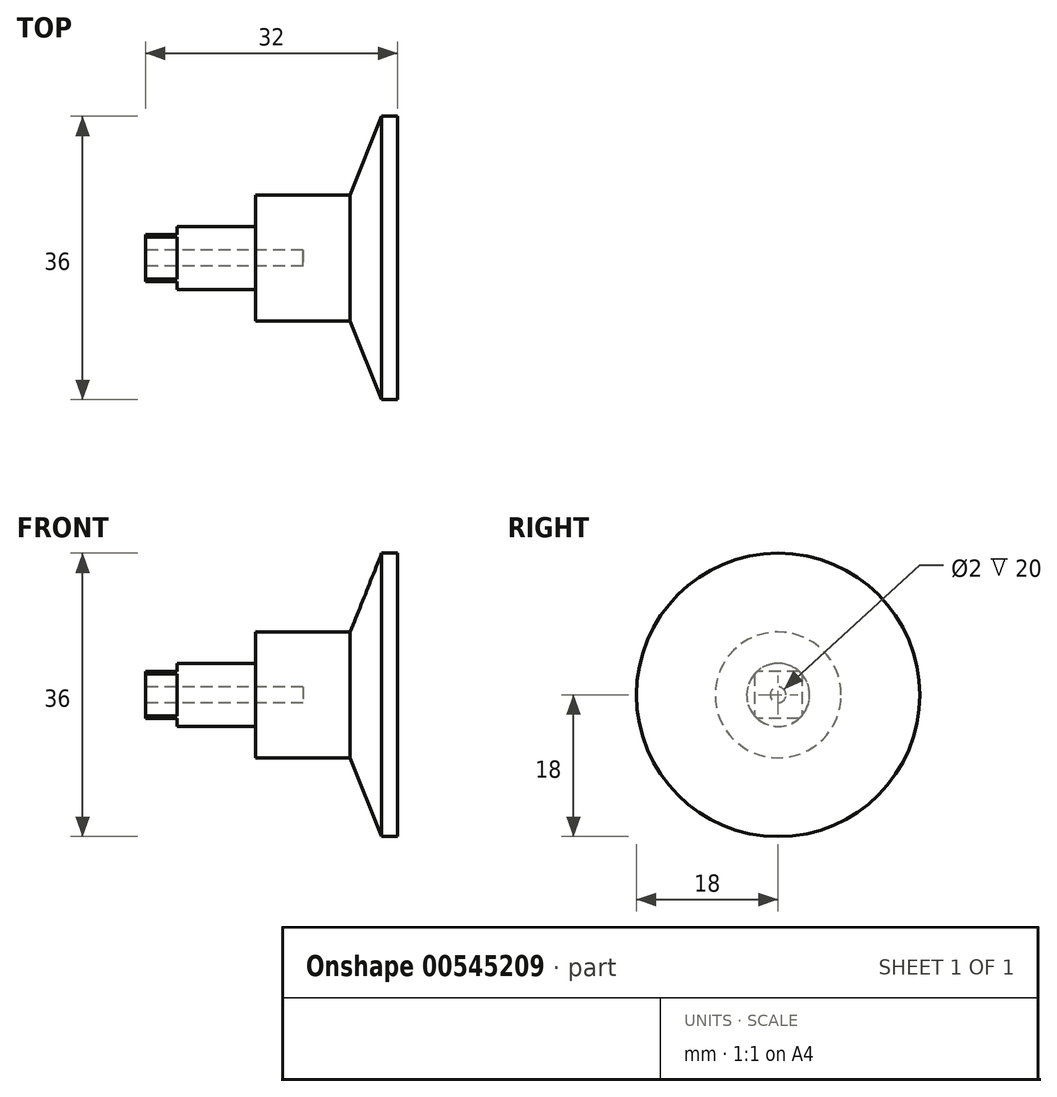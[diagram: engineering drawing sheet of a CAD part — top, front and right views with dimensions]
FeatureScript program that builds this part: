
annotation { "Feature Type Name" : "Feature", "Feature Type Description" : "" }
export const myFeature = defineFeature(function(context is Context, id is Id, definition is map)
    precondition{}
    {
        {
            var Q0;
            Q0=qCreatedBy(makeId("Front.planeOp"),FACE);
            var sketch = newSketch(context, id + "F0", { "sketchPlane" : qUnion([Q0])});
            skLineSegment(sketch, "E0", {"start": v(-44.44, 0) * mm, "end": v(44.44, 0) * mm, "construction": true});
            skLineSegment(sketch, "E1", {"start": v(-18, 8) * mm, "end": v(-6, 8) * mm});
            skLineSegment(sketch, "E2", {"start": v(-6, 8) * mm, "end": v(-2, 18) * mm});
            skLineSegment(sketch, "E3", {"start": v(-2, 18) * mm, "end": v(0, 18) * mm});
            skLineSegment(sketch, "E4", {"start": v(0, 18) * mm, "end": v(0, 0) * mm});
            skLineSegment(sketch, "E5", {"start": v(0, 0) * mm, "end": v(-12, 0) * mm});
            skLineSegment(sketch, "E6", {"start": v(-12, 0) * mm, "end": v(-12, 1) * mm});
            skLineSegment(sketch, "E7", {"start": v(-12, 1) * mm, "end": v(-32, 1) * mm});
            skLineSegment(sketch, "E8", {"start": v(-32, 1) * mm, "end": v(-32, 4) * mm});
            skLineSegment(sketch, "E9", {"start": v(-32, 4) * mm, "end": v(-18, 4) * mm});
            skLineSegment(sketch, "E10", {"start": v(-18, 4) * mm, "end": v(-18, 8) * mm});
            skSolve(sketch);
        }
        {
            var Q0;
            Q0 = qSketchRegion(id + "F0", true);
            var Q1;
            Q1=sQuery(id+"F0.wireOp",EDGE,"E0");
            revolve(context, id + "F1", {"entities" : qUnion([Q0]), "axis" : qUnion([Q1]), "revolveType" : RevolveType.FULL});
        }
        {
            var Q0;
            Q0=makeQuery(id+"F1.opRevolve","SWEPT_FACE",FACE,{"disambiguationData":[OSD([sQuery(id+"F0.wireOp",EDGE,"E8")])]});
            var sketch = newSketch(context, id + "F2", { "sketchPlane" : qUnion([Q0])});
            skLineSegment(sketch, "E11.bottom", {"start": v(-3, 3) * mm, "end": v(3, 3) * mm});
            skLineSegment(sketch, "E11.top", {"start": v(-3, -3) * mm, "end": v(3, -3) * mm});
            skLineSegment(sketch, "E11.left", {"start": v(-3, 3) * mm, "end": v(-3, -3) * mm});
            skLineSegment(sketch, "E11.right", {"start": v(3, 3) * mm, "end": v(3, -3) * mm});
            skCircle(sketch, "E12.0", {"center": v(0, 0) * mm, "radius": 4 * mm});
            skLineSegment(sketch, "E13", {"start": v(-3, -3) * mm, "end": v(3, 3) * mm, "construction": true});
            skSolve(sketch);
        }
        {
            var Q0;
            Q0=makeQuery(id+"F2.imprint","IMPRINT",FACE,{"disambiguationData":[TD([[makeQuery(id+"F2.imprint","IMPRINT",EDGE,{"derivedFrom":makeQuery(id+"F1.opRevolve","SWEPT_EDGE",EDGE,{"disambiguationData":[OSD([sQuery(id+"F0.wireOp",EDGE,"E7"),sQuery(id+"F0.wireOp",EDGE,"E8")])]})}),1.0]])]});
            var Q1;
            Q1=makeQuery(id+"F2.imprint","IMPRINT",FACE,{"disambiguationData":[TD([[makeQuery(id+"F2.imprint","IMPRINT",EDGE,{"derivedFrom":sQuery(id+"F2.wireOp",EDGE,"E11.bottom")}),1.0]])]});
            var Q2;
            {var subQ0=sQuery(id+"F2.wireOp",EDGE,"E12.0");var subQ1=sQuery(id+"F2.wireOp",EDGE,"E11.right");var subQ2=makeQuery(id+"F2.imprint","INTERSECT",VERTEX,{"disambiguationData":[OD(0.0)],"derivedFrom":[subQ1,subQ0]});Q2=makeQuery(id+"F2.imprint","IMPRINT",FACE,{"disambiguationData":[TD([[makeQuery(id+"F2.imprint","IMPRINT",EDGE,{"disambiguationData":[TD([[subQ2,-1.0]])],"derivedFrom":subQ1}),1.0]])]});}
            var Q3;
            {var subQ0=sQuery(id+"F2.wireOp",EDGE,"E12.0");var subQ1=sQuery(id+"F2.wireOp",EDGE,"E11.top");var subQ2=makeQuery(id+"F2.imprint","INTERSECT",VERTEX,{"disambiguationData":[OD(0.0)],"derivedFrom":[subQ1,subQ0]});Q3=makeQuery(id+"F2.imprint","IMPRINT",FACE,{"disambiguationData":[TD([[makeQuery(id+"F2.imprint","IMPRINT",EDGE,{"disambiguationData":[TD([[subQ2,-1.0]])],"derivedFrom":subQ1}),-1.0]])]});}
            var Q4;
            {var subQ0=sQuery(id+"F2.wireOp",EDGE,"E12.0");var subQ1=sQuery(id+"F2.wireOp",EDGE,"E11.left");var subQ2=makeQuery(id+"F2.imprint","INTERSECT",VERTEX,{"disambiguationData":[OD(0.0)],"derivedFrom":[subQ1,subQ0]});Q4=makeQuery(id+"F2.imprint","IMPRINT",FACE,{"disambiguationData":[TD([[makeQuery(id+"F2.imprint","IMPRINT",EDGE,{"disambiguationData":[TD([[subQ2,-1.0]])],"derivedFrom":subQ1}),-1.0]])]});}
            extrude(context, id + "F3", {"entities" : qUnion([Q0, Q1, Q2, Q3, Q4]), "operationType" : NewBodyOperationType.REMOVE, "oppositeDirection" : true, "depth" : 4 * mm, "offsetDistance" : 25 * mm});
        }
    });
